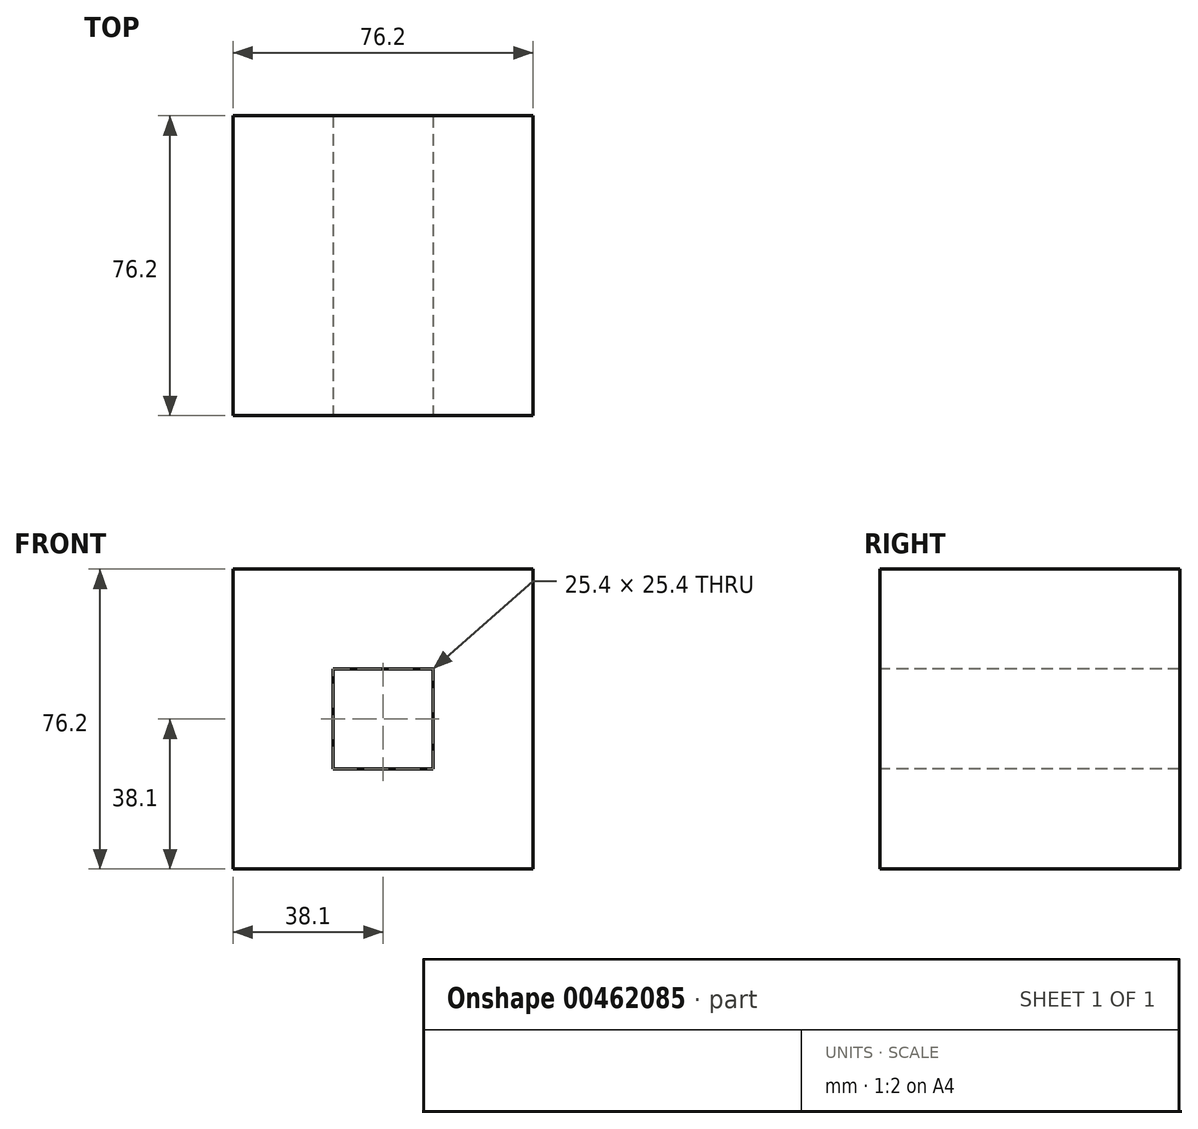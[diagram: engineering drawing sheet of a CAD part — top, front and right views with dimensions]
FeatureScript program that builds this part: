
annotation { "Feature Type Name" : "Feature", "Feature Type Description" : "" }
export const myFeature = defineFeature(function(context is Context, id is Id, definition is map)
    precondition{}
    {
        {
            var Q0;
            Q0=qCreatedBy(makeId("Front.planeOp"),FACE);
            var sketch = newSketch(context, id + "F0", { "sketchPlane" : qUnion([Q0])});
            skLineSegment(sketch, "E0.bottom", {"start": v(38.1, -38.1) * mm, "end": v(-38.1, -38.1) * mm});
            skLineSegment(sketch, "E0.top", {"start": v(38.1, 38.1) * mm, "end": v(-38.1, 38.1) * mm});
            skLineSegment(sketch, "E0.left", {"start": v(38.1, -38.1) * mm, "end": v(38.1, 38.1) * mm});
            skLineSegment(sketch, "E0.right", {"start": v(-38.1, -38.1) * mm, "end": v(-38.1, 38.1) * mm});
            skPoint(sketch, "E0.middle", {"position": v(0, 0) * mm});
            skSolve(sketch);
        }
        {
            var Q0;
            Q0 = qSketchRegion(id + "F0", true);
            extrude(context, id + "F1", {"entities" : qUnion([Q0]), "depth" : 76.2 * mm});
        }
        {
            var Q0;
            Q0=makeQuery(id+"F1.opExtrude","CAP_FACE",FACE,{"disambiguationData":[OSD([sQuery(id+"F0.wireOp",EDGE,"E0.bottom"),sQuery(id+"F0.wireOp",EDGE,"E0.top"),sQuery(id+"F0.wireOp",EDGE,"E0.left"),sQuery(id+"F0.wireOp",EDGE,"E0.right")])],"isStart":false});
            var sketch = newSketch(context, id + "F2", { "sketchPlane" : qUnion([Q0])});
            skLineSegment(sketch, "E1.bottom", {"start": v(12.7, -12.7) * mm, "end": v(-12.7, -12.7) * mm});
            skLineSegment(sketch, "E1.top", {"start": v(12.7, 12.7) * mm, "end": v(-12.7, 12.7) * mm});
            skLineSegment(sketch, "E1.left", {"start": v(12.7, -12.7) * mm, "end": v(12.7, 12.7) * mm});
            skLineSegment(sketch, "E1.right", {"start": v(-12.7, -12.7) * mm, "end": v(-12.7, 12.7) * mm});
            skPoint(sketch, "E1.middle", {"position": v(0, 0) * mm});
            skSolve(sketch);
        }
        {
            var Q0;
            Q0=makeQuery(id+"F2.imprint","IMPRINT",FACE,{"disambiguationData":[TD([[makeQuery(id+"F2.imprint","IMPRINT",EDGE,{"derivedFrom":sQuery(id+"F2.wireOp",EDGE,"E1.bottom")}),-1.0]])]});
            extrude(context, id + "F3", {"entities" : qUnion([Q0]), "operationType" : NewBodyOperationType.REMOVE, "oppositeDirection" : true, "depth" : 25.4 * mm});
        }
        {
            var Q0;
            Q0=makeQuery(id+"F1.opExtrude","CAP_FACE",FACE,{"disambiguationData":[OSD([sQuery(id+"F0.wireOp",EDGE,"E0.bottom"),sQuery(id+"F0.wireOp",EDGE,"E0.top"),sQuery(id+"F0.wireOp",EDGE,"E0.left"),sQuery(id+"F0.wireOp",EDGE,"E0.right")])],"isStart":true});
            var sketch = newSketch(context, id + "F4", { "sketchPlane" : qUnion([Q0])});
            skLineSegment(sketch, "E2.bottom", {"start": v(12.7, -12.7) * mm, "end": v(-12.7, -12.7) * mm});
            skLineSegment(sketch, "E2.top", {"start": v(12.7, 12.7) * mm, "end": v(-12.7, 12.7) * mm});
            skLineSegment(sketch, "E2.left", {"start": v(12.7, -12.7) * mm, "end": v(12.7, 12.7) * mm});
            skLineSegment(sketch, "E2.right", {"start": v(-12.7, -12.7) * mm, "end": v(-12.7, 12.7) * mm});
            skPoint(sketch, "E2.middle", {"position": v(0, 0) * mm});
            skSolve(sketch);
        }
        {
            var Q0;
            Q0=makeQuery(id+"F4.imprint","IMPRINT",FACE,{"disambiguationData":[TD([[makeQuery(id+"F4.imprint","IMPRINT",EDGE,{"derivedFrom":sQuery(id+"F4.wireOp",EDGE,"E2.bottom")}),-1.0]])]});
            extrude(context, id + "F5", {"entities" : qUnion([Q0]), "operationType" : NewBodyOperationType.REMOVE, "oppositeDirection" : true, "depth" : 50.8 * mm});
        }
    });
